# Revit family: LB6A
name_source: partatom
category: Lighting Fixtures
revit_build: Autodesk Revit 2014 (Build: 20130308_1515(x64)
units: mm (PartAtom-declared; Revit-internal decimal feet)

## types (1)
- LB6A
    Apparent Load = 10 VA
    Color Filter = 16777215
    Default Elevation = 48"
    Description = 6in Fixed or Directional Downlight
    Dimming Lamp Color Temperature Shift = <None>
    Emit Shape Visible in Rendering = No
    Emit from Circle Diameter = 6"
    Glass = Hubbell-White Glass
    Input Wattage = 10 W
    Lamp = LED
    Load Classification = Lighting
    Manufacturer = Prescolite
    Model = LB6A
    More Photometric Web Link = https://www.hubbell.com
    Photometric Web File = LB6A7L30K9_WH.ies
    Power Factor = 1
    Product Documentation Link = https://hubbellcdn.com
    Product Page URL = https://www.hubbell.com
    Tilt Angle = -90.00°
    Trim = Hubbell-White
    URL = https://www.hubbell.com
    Voltage = 120 V
    Wattage Comments = Energy saving LED light engine with 10-watt input power

## geometry (parser evidence)
native form markers: Blend x6, Sweep x1
no freeform markers — native parametric forms only
